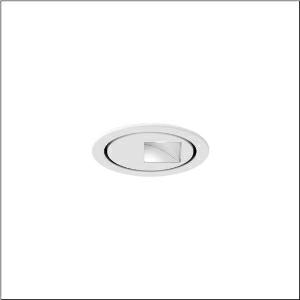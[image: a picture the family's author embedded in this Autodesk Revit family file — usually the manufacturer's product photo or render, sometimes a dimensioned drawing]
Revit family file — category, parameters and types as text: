
# Revit family: lunis_11_micro_round_51dj11cd1wf21
name_source: partatom
category: Lighting Fixtures
units: mm (PartAtom-declared; Revit-internal decimal feet)

## family parameters
Cut with Voids When Loaded = No
Host = Face
Light Source = No
Part Type = Normal
Room Calculation Point = No
Round Connector Dimension = Use Diameter
Shared = No

## types (1)
- Lunis 11 micro round (1 x LED 3000K / CRI = 80 (unbekannt), 1320 lm, 3000K)
    Apparent Load = 20 VA
    CIE Flux Codes = 42 75 96 100 100
    Color Rendering = 80
    Color Temperature = 3000K
    Default Elevation = 1800 mm
    Description = Lunis 11 micro round, downlight, light control with wallwasher, of highly reflective aluminium, highly specular, light emission: direct distribution, LED rated luminous flux: 1.320lm, light colour: 830, with terminal, 5-pole, mains connection: 220..230V, AC, 50/60Hz, LED module, of aluminium, highly specular, white, diameter: 114mm, clamping range: 1..40mm, recessing ring, of plastic, traffic white (RAL 9016), protection rating (complete): IP20, insulation class (complete): insulation class II (safety insulation), certification: CE, permissible ambient temperature for indoor applications: 0..+35°C, packaging unit: 1 piece
    Height = 0 mm  [stored 0 ft]
    Lamp = 1 x LED 3000K / CRI >= 80 (unbekannt)
    Lamp Light Flux = 1320 lm
    Lamp count = 1
    Length = 114 mm
    Luminous efficacy = 67 lm/W
    Manufacturer = Siteco
    ModVariant = No
    Model = 51DJ11CD1WF21
    Mounting Place = Ceiling
    Mounting Type = Recessed
    Number of Poles = 1
    OnlyDefault = Yes
    Power Factor = 1
    Product Name = Lunis 11 micro round
    Product group = downlight
    ProductGroupID = 400
    Protection Class = Protection class II
    Protection Degree = IP 20
    RLX_Detail_Level = 1
    RLX_Emergency_Light_Flux = 0 lm
    RLX_Emergency_Type = 0
    RLX_Emergency_Type_DB = No
    RlxData = <blob elided: 40773 chars, md5=33947d7b>
    Socket = socket
    Standby Power = 0 W
    System Light Flux = 1320 lm
    System Power = 20 W
    Type Comments = Product without accessories
    Type Image = l_1004773.jpg
    URL = http://relux.com
    VarID = ---
    Voltage = 0 V
    Weight = 0.00 kg
    Width = 114 mm

note: [stored X ft] marks values corroborated as IEEE doubles in the binary element streams (Revit-internal decimal feet)

## geometry (parser evidence)
native form markers: Blend x4, Sweep x9
no freeform markers — native parametric forms only
